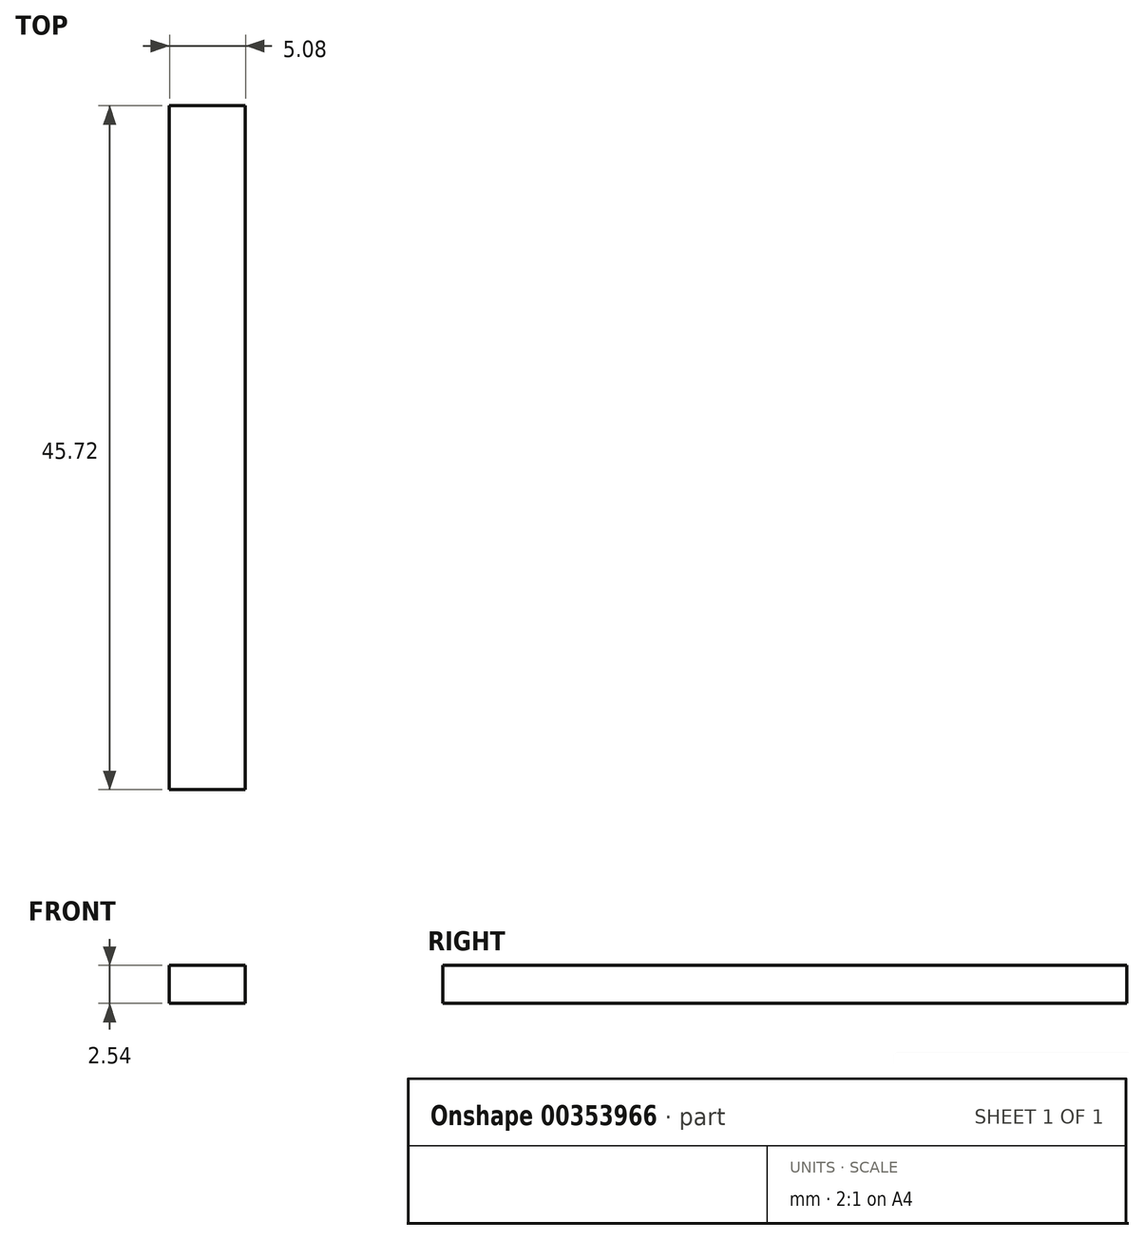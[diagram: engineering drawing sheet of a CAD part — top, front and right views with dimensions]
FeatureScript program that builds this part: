
annotation { "Feature Type Name" : "Feature", "Feature Type Description" : "" }
export const myFeature = defineFeature(function(context is Context, id is Id, definition is map)
    precondition{}
    {
        {
            var Q0;
            Q0=qCreatedBy(makeId("Top.planeOp"),FACE);
            var sketch = newSketch(context, id + "F0", { "sketchPlane" : qUnion([Q0])});
            skLineSegment(sketch, "E0.bottom", {"start": v(-14, 20.3) * mm, "end": v(-8.92, 20.3) * mm});
            skLineSegment(sketch, "E0.top", {"start": v(-14, -25.42) * mm, "end": v(-8.92, -25.42) * mm});
            skLineSegment(sketch, "E0.left", {"start": v(-14, 20.3) * mm, "end": v(-14, -25.42) * mm});
            skLineSegment(sketch, "E0.right", {"start": v(-8.92, 20.3) * mm, "end": v(-8.92, -25.42) * mm});
            skSolve(sketch);
        }
        {
            var Q0;
            Q0 = qSketchRegion(id + "F0", true);
            extrude(context, id + "F1", {"entities" : qUnion([Q0]), "depth" : 2.54 * mm});
        }
    });
